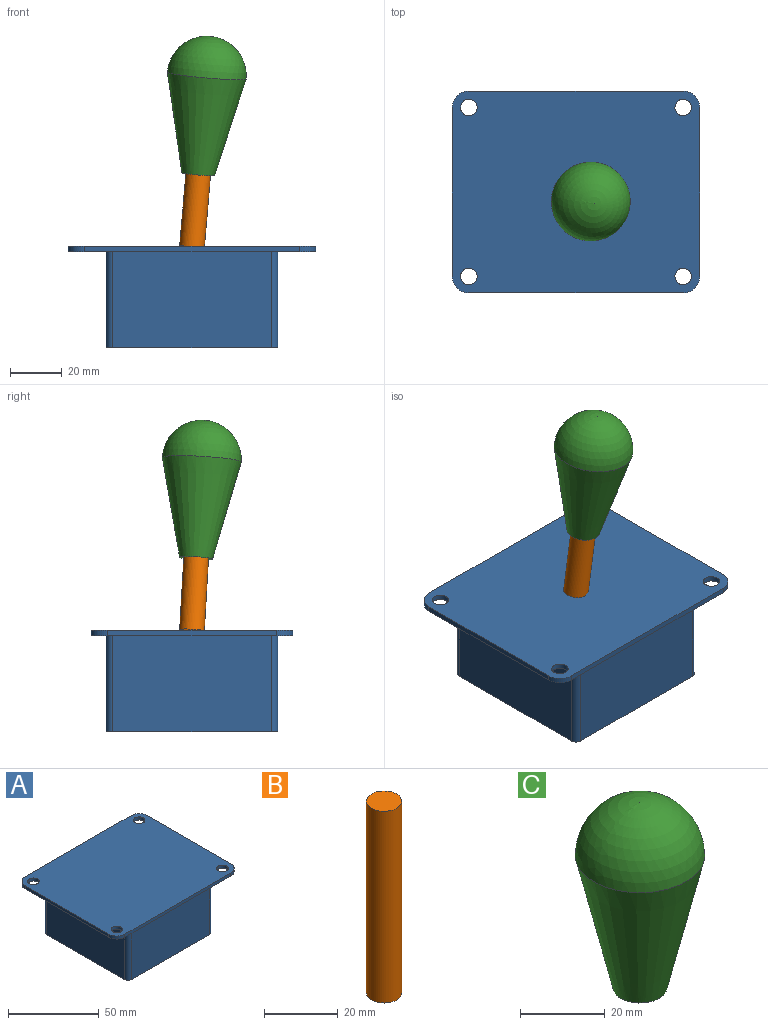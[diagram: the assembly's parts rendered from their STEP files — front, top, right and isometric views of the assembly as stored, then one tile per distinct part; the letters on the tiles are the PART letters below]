
ASSEMBLY  parts=3 mates=2
PART A: 23 faces, bbox 95.3x77.8x39.1 mm
  f0: plane 65.09x2.03mm, normal (-1,0,0), area 132.3mm2, adj f1,f11,f12,f13
  f1: cylinder r=6.35mm len=6.35mm, axis (0,0,1), area 20.3mm2, adj f0,f2,f12,f13
  f2: plane 82.55x2.03mm, normal (0,-1,0), area 167.7mm2, adj f1,f3,f12,f13
  f3: cylinder r=6.35mm len=6.35mm, axis (0,0,1), area 20.3mm2, adj f2,f4,f12,f13
  f4: plane 65.09x2.03mm, normal (1,0,0), area 132.3mm2, adj f3,f5,f12,f13
  f5: cylinder r=6.35mm len=6.35mm, axis (0,0,1), area 20.3mm2, adj f4,f6,f12,f13
  f6: plane 82.55x2.03mm, normal (0,1,0), area 167.7mm2, adj f5,f11,f12,f13
  f7: cylinder r=3.17mm len=6.35mm, axis (0,0,1), area 40.5mm2, adj f12,f13
  f8: cylinder r=3.17mm len=6.35mm, axis (0,0,1), area 40.5mm2, adj f12,f13
  f9: cylinder r=3.17mm len=6.35mm, axis (0,0,1), area 40.5mm2, adj f12,f13
  f10: cylinder r=3.17mm len=6.35mm, axis (0,0,1), area 40.5mm2, adj f12,f13
  f11: cylinder r=6.35mm len=6.35mm, axis (0,0,1), area 20.3mm2, adj f0,f6,f12,f13
  f12: plane 95.25x77.79mm, normal (0,0,-1), area 2892.2mm2, adj f0,f1,f2,f3,f4,f5,f6,f7
  f13: plane 95.25x77.79mm, normal (0,0,1), area 7248mm2, adj f0,f1,f2,f3,f4,f5,f6,f7
  f14: plane 60.96x37.08mm, normal (-1,0,0), area 2260.6mm2, adj f12,f15,f21,f22
  f15: cylinder r=2.54mm len=37.08mm, axis (0,0,1), area 148mm2, adj f12,f14,f16,f22
  f16: plane 60.96x37.08mm, normal (0,1,0), area 2260.6mm2, adj f12,f15,f17,f22
  f17: cylinder r=2.54mm len=37.08mm, axis (0,0,1), area 148mm2, adj f12,f16,f18,f22
  f18: plane 60.96x37.08mm, normal (1,0,0), area 2260.6mm2, adj f12,f17,f19,f22
  f19: cylinder r=2.54mm len=37.08mm, axis (0,0,1), area 148mm2, adj f12,f18,f20,f22
  f20: plane 60.96x37.08mm, normal (0,-1,0), area 2260.6mm2, adj f12,f19,f21,f22
  f21: cylinder r=2.54mm len=37.08mm, axis (0,0,1), area 148mm2, adj f12,f14,f20,f22
  f22: plane 66.04x66.04mm, normal (0,0,-1), area 4355.7mm2, adj f14,f15,f16,f17,f18,f19,f20,f21
PART B: 3 faces, bbox 9.5x9.5x63.5 mm
  f0: cylinder r=4.76mm len=63.5mm, axis (0,0,-1), area 1900.2mm2, adj f1,f2
  f1: plane 9.53x9.53mm, normal (0,0,1), area 71.3mm2, adj f0
  f2: plane 9.53x9.53mm, normal (0,0,-1), area 71.3mm2, adj f0
PART C: 3 faces, bbox 30.5x30.5x53.3 mm
  f0: plane 12.7x12.7mm, normal (0,0,-1), area 126.7mm2, adj f1
  f1: cone r=15.24mm half-angle=13.1deg, axis (0,0,1), area 2653.6mm2, adj f0,f2
  f2: sphere r=15.24mm, area 1459.3mm2, adj f1
PLACE A t=(3.74,-19.87,7.92)mm fixed
PLACE B rot(axis=(0.29,0.52,-0.8),9.9deg) t=(-51.41,-83.21,9.06)mm
PLACE C rot(axis=(0.29,0.52,-0.8),9.9deg) t=(-49.65,-13.77,40.98)mm
MATE fastened C.f1 <-> B.f0  axis (0.09,-0.06,0.99) through (9.42,-23.64,73.61)mm
MATE ball B.f0 <-> A.f13  axis (-0.09,0.06,-0.99) through (3.74,-19.87,7.92)mm
